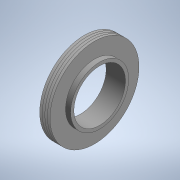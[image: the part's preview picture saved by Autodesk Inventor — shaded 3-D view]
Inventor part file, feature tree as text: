
AUTODESK INVENTOR PART (.ipt)
format: ipt  version: 2020 (Build 240168000, 168)  size: 154,624 bytes
history: native  units: mm
features: revolve x1, sketch x1
ambient origin geometry x8: Origin, YZ Plane, XZ Plane, XY Plane, X Axis, Y Axis, Z Axis, Center Point
bodies: 实体1 (feature_tree)
feature tree (2):
  revolve  "旋转1"  [1 undecoded]
  sketch  "草图1"  dims[d0=40.0mm d1=45.0mm d2=15.0mm d3=3.0mm d4=8.0mm d5=34.5mm d6=2.0mm d7=60.0deg d8=2.0mm d9=2.0mm d10=2.0mm d11=60.0deg d12=60.0deg d13=60.0deg d14=22.5mm d15=90.0deg]
note: 1 required parameter value undecoded (feature->parameter linkage not recoverable at this tier; creation-order binding heuristic only, values carry confidence <= 0.55)
